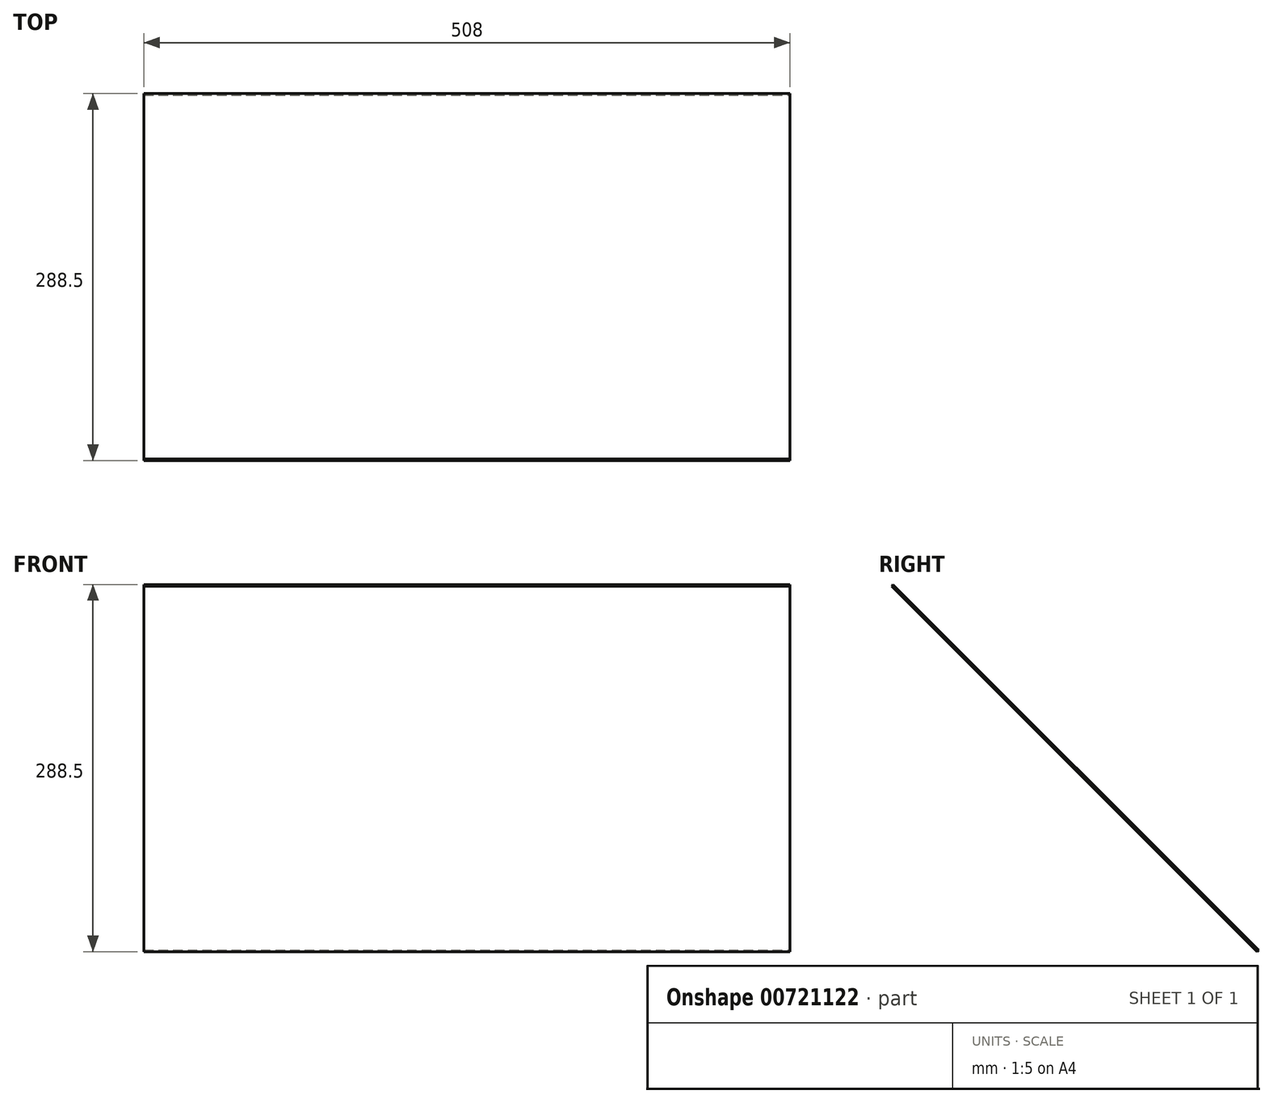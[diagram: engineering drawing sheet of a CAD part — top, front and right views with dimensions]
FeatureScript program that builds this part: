
annotation { "Feature Type Name" : "Feature", "Feature Type Description" : "" }
export const myFeature = defineFeature(function(context is Context, id is Id, definition is map)
    precondition{}
    {
        {
            var Q0;
            Q0=qCreatedBy(makeId("Front.planeOp"),FACE);
            var sketch = newSketch(context, id + "F0", { "sketchPlane" : qUnion([Q0])});
            skLineSegment(sketch, "E0", {"start": v(0, 0) * mm, "end": v(508, 0) * mm});
            skSolve(sketch);
        }
        {
            var Q0;
            Q0=sQuery(id+"F0.wireOp",EDGE,"E0");
            cPlane(context, id + "F1", {"entities" : qUnion([Q0]), "cplaneType" : CPlaneType.LINE_ANGLE, "offset" : 25.4 * mm, "angle" : 45 * degree, "width" : 152.4 * mm, "height" : 152.4 * mm});
        }
        {
            var Q0;
            Q0=qCreatedBy(id+"F1.planeOp",FACE);
            var sketch = newSketch(context, id + "F2", { "sketchPlane" : qUnion([Q0])});
            skLineSegment(sketch, "E1.bottom", {"start": v(0, 0) * mm, "end": v(-508, 0) * mm});
            skLineSegment(sketch, "E1.top", {"start": v(0, 406.4) * mm, "end": v(-508, 406.4) * mm});
            skLineSegment(sketch, "E1.left", {"start": v(0, 0) * mm, "end": v(0, 406.4) * mm});
            skLineSegment(sketch, "E1.right", {"start": v(-508, 0) * mm, "end": v(-508, 406.4) * mm});
            skSolve(sketch);
        }
        {
            var Q0;
            Q0 = qSketchRegion(id + "F2", true);
            extrude(context, id + "F3", {"entities" : qUnion([Q0]), "depth" : 1.6 * mm, "offsetDistance" : 25.4 * mm});
        }
    });
